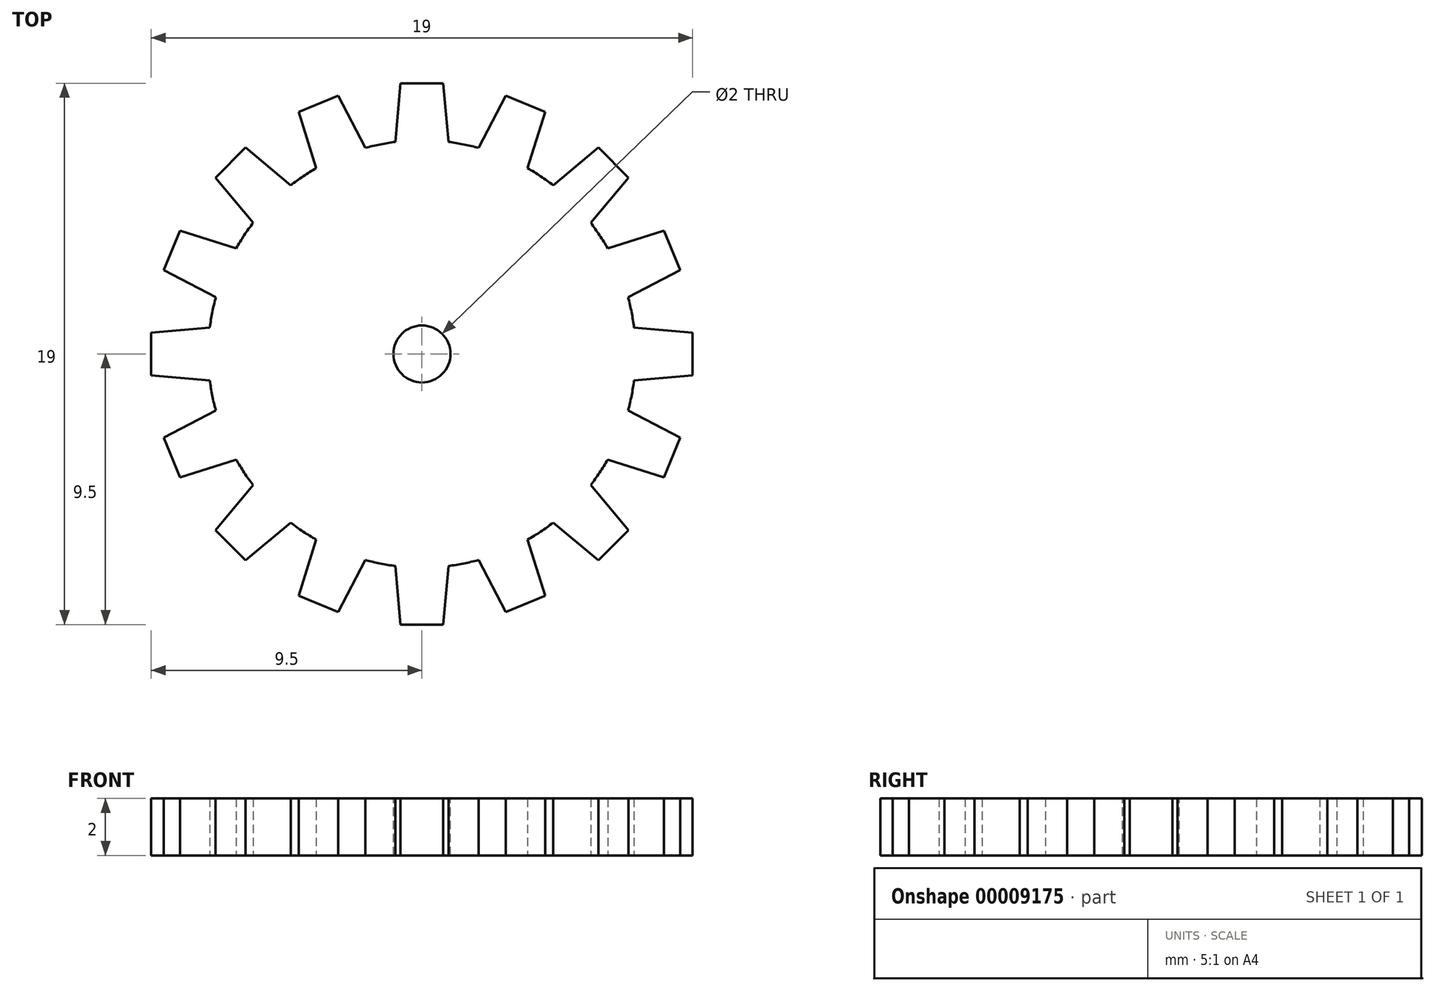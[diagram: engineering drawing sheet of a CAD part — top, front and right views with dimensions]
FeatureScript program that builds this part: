
annotation { "Feature Type Name" : "Feature", "Feature Type Description" : "" }
export const myFeature = defineFeature(function(context is Context, id is Id, definition is map)
    precondition{}
    {
        {
            var Q0;
            Q0=qCreatedBy(makeId("Top.planeOp"),FACE);
            var sketch = newSketch(context, id + "F0", { "sketchPlane" : qUnion([Q0])});
            skCircle(sketch, "E0", {"center": v(0, 0) * mm, "radius": 7.5 * mm});
            skLineSegment(sketch, "E1", {"start": v(0, 0) * mm, "end": v(0, 7.5) * mm, "construction": true});
            skLineSegment(sketch, "E2", {"start": v(-0.93, 7.44) * mm, "end": v(-0.75, 9.5) * mm});
            skLineSegment(sketch, "E3", {"start": v(-0.75, 9.5) * mm, "end": v(0, 9.5) * mm});
            skLineSegment(sketch, "E4.MirrorCS", {"start": v(0.93, 7.44) * mm, "end": v(0.75, 9.5) * mm});
            skLineSegment(sketch, "E5.MirrorCS", {"start": v(0.75, 9.5) * mm, "end": v(0, 9.5) * mm});
            skLineSegment(sketch, "E6.1.0", {"start": v(-3.7, 6.52) * mm, "end": v(-4.33, 8.49) * mm});
            skLineSegment(sketch, "E6.1.1", {"start": v(-4.33, 8.49) * mm, "end": v(-3.64, 8.78) * mm});
            skLineSegment(sketch, "E6.1.2", {"start": v(-2.94, 9.06) * mm, "end": v(-3.64, 8.78) * mm});
            skLineSegment(sketch, "E6.1.3", {"start": v(-1.99, 7.23) * mm, "end": v(-2.94, 9.06) * mm});
            skLineSegment(sketch, "E6.2.0", {"start": v(-5.92, 4.6) * mm, "end": v(-7.25, 6.19) * mm});
            skLineSegment(sketch, "E6.2.1", {"start": v(-7.25, 6.19) * mm, "end": v(-6.72, 6.72) * mm});
            skLineSegment(sketch, "E6.2.2", {"start": v(-6.19, 7.25) * mm, "end": v(-6.72, 6.72) * mm});
            skLineSegment(sketch, "E6.2.3", {"start": v(-4.6, 5.92) * mm, "end": v(-6.19, 7.25) * mm});
            skLineSegment(sketch, "E6.3.0", {"start": v(-7.23, 1.99) * mm, "end": v(-9.06, 2.94) * mm});
            skLineSegment(sketch, "E6.3.1", {"start": v(-9.06, 2.94) * mm, "end": v(-8.78, 3.64) * mm});
            skLineSegment(sketch, "E6.3.2", {"start": v(-8.49, 4.33) * mm, "end": v(-8.78, 3.64) * mm});
            skLineSegment(sketch, "E6.3.3", {"start": v(-6.52, 3.7) * mm, "end": v(-8.49, 4.33) * mm});
            skLineSegment(sketch, "E6.4.0", {"start": v(-7.44, -0.93) * mm, "end": v(-9.5, -0.75) * mm});
            skLineSegment(sketch, "E6.4.1", {"start": v(-9.5, -0.75) * mm, "end": v(-9.5, 0) * mm});
            skLineSegment(sketch, "E6.4.2", {"start": v(-9.5, 0.75) * mm, "end": v(-9.5, 0) * mm});
            skLineSegment(sketch, "E6.4.3", {"start": v(-7.44, 0.93) * mm, "end": v(-9.5, 0.75) * mm});
            skLineSegment(sketch, "E6.5.0", {"start": v(-6.52, -3.7) * mm, "end": v(-8.49, -4.33) * mm});
            skLineSegment(sketch, "E6.5.1", {"start": v(-8.49, -4.33) * mm, "end": v(-8.78, -3.64) * mm});
            skLineSegment(sketch, "E6.5.2", {"start": v(-9.06, -2.94) * mm, "end": v(-8.78, -3.64) * mm});
            skLineSegment(sketch, "E6.5.3", {"start": v(-7.23, -1.99) * mm, "end": v(-9.06, -2.94) * mm});
            skLineSegment(sketch, "E6.6.0", {"start": v(-4.6, -5.92) * mm, "end": v(-6.19, -7.25) * mm});
            skLineSegment(sketch, "E6.6.1", {"start": v(-6.19, -7.25) * mm, "end": v(-6.72, -6.72) * mm});
            skLineSegment(sketch, "E6.6.2", {"start": v(-7.25, -6.19) * mm, "end": v(-6.72, -6.72) * mm});
            skLineSegment(sketch, "E6.6.3", {"start": v(-5.92, -4.6) * mm, "end": v(-7.25, -6.19) * mm});
            skLineSegment(sketch, "E6.7.0", {"start": v(-1.99, -7.23) * mm, "end": v(-2.94, -9.06) * mm});
            skLineSegment(sketch, "E6.7.1", {"start": v(-2.94, -9.06) * mm, "end": v(-3.64, -8.78) * mm});
            skLineSegment(sketch, "E6.7.2", {"start": v(-4.33, -8.49) * mm, "end": v(-3.64, -8.78) * mm});
            skLineSegment(sketch, "E6.7.3", {"start": v(-3.7, -6.52) * mm, "end": v(-4.33, -8.49) * mm});
            skLineSegment(sketch, "E6.8.0", {"start": v(0.93, -7.44) * mm, "end": v(0.75, -9.5) * mm});
            skLineSegment(sketch, "E6.8.1", {"start": v(0.75, -9.5) * mm, "end": v(0, -9.5) * mm});
            skLineSegment(sketch, "E6.8.2", {"start": v(-0.75, -9.5) * mm, "end": v(0, -9.5) * mm});
            skLineSegment(sketch, "E6.8.3", {"start": v(-0.93, -7.44) * mm, "end": v(-0.75, -9.5) * mm});
            skLineSegment(sketch, "E6.9.0", {"start": v(3.7, -6.52) * mm, "end": v(4.33, -8.49) * mm});
            skLineSegment(sketch, "E6.9.1", {"start": v(4.33, -8.49) * mm, "end": v(3.64, -8.78) * mm});
            skLineSegment(sketch, "E6.9.2", {"start": v(2.94, -9.06) * mm, "end": v(3.64, -8.78) * mm});
            skLineSegment(sketch, "E6.9.3", {"start": v(1.99, -7.23) * mm, "end": v(2.94, -9.06) * mm});
            skLineSegment(sketch, "E6.10.0", {"start": v(5.92, -4.6) * mm, "end": v(7.25, -6.19) * mm});
            skLineSegment(sketch, "E6.10.1", {"start": v(7.25, -6.19) * mm, "end": v(6.72, -6.72) * mm});
            skLineSegment(sketch, "E6.10.2", {"start": v(6.19, -7.25) * mm, "end": v(6.72, -6.72) * mm});
            skLineSegment(sketch, "E6.10.3", {"start": v(4.6, -5.92) * mm, "end": v(6.19, -7.25) * mm});
            skLineSegment(sketch, "E6.11.0", {"start": v(7.23, -1.99) * mm, "end": v(9.06, -2.94) * mm});
            skLineSegment(sketch, "E6.11.1", {"start": v(9.06, -2.94) * mm, "end": v(8.78, -3.64) * mm});
            skLineSegment(sketch, "E6.11.2", {"start": v(8.49, -4.33) * mm, "end": v(8.78, -3.64) * mm});
            skLineSegment(sketch, "E6.11.3", {"start": v(6.52, -3.7) * mm, "end": v(8.49, -4.33) * mm});
            skLineSegment(sketch, "E6.12.0", {"start": v(7.44, 0.93) * mm, "end": v(9.5, 0.75) * mm});
            skLineSegment(sketch, "E6.12.1", {"start": v(9.5, 0.75) * mm, "end": v(9.5, 0) * mm});
            skLineSegment(sketch, "E6.12.2", {"start": v(9.5, -0.75) * mm, "end": v(9.5, 0) * mm});
            skLineSegment(sketch, "E6.12.3", {"start": v(7.44, -0.93) * mm, "end": v(9.5, -0.75) * mm});
            skLineSegment(sketch, "E6.13.0", {"start": v(6.52, 3.7) * mm, "end": v(8.49, 4.33) * mm});
            skLineSegment(sketch, "E6.13.1", {"start": v(8.49, 4.33) * mm, "end": v(8.78, 3.64) * mm});
            skLineSegment(sketch, "E6.13.2", {"start": v(9.06, 2.94) * mm, "end": v(8.78, 3.64) * mm});
            skLineSegment(sketch, "E6.13.3", {"start": v(7.23, 1.99) * mm, "end": v(9.06, 2.94) * mm});
            skLineSegment(sketch, "E6.14.0", {"start": v(4.6, 5.92) * mm, "end": v(6.19, 7.25) * mm});
            skLineSegment(sketch, "E6.14.1", {"start": v(6.19, 7.25) * mm, "end": v(6.72, 6.72) * mm});
            skLineSegment(sketch, "E6.14.2", {"start": v(7.25, 6.19) * mm, "end": v(6.72, 6.72) * mm});
            skLineSegment(sketch, "E6.14.3", {"start": v(5.92, 4.6) * mm, "end": v(7.25, 6.19) * mm});
            skLineSegment(sketch, "E6.15.0", {"start": v(1.99, 7.23) * mm, "end": v(2.94, 9.06) * mm});
            skLineSegment(sketch, "E6.15.1", {"start": v(2.94, 9.06) * mm, "end": v(3.64, 8.78) * mm});
            skLineSegment(sketch, "E6.15.2", {"start": v(4.33, 8.49) * mm, "end": v(3.64, 8.78) * mm});
            skLineSegment(sketch, "E6.15.3", {"start": v(3.7, 6.52) * mm, "end": v(4.33, 8.49) * mm});
            skSolve(sketch);
        }
        {
            var Q0;
            Q0 = qSketchRegion(id + "F0", true);
            extrude(context, id + "F1", {"entities" : qUnion([Q0]), "depth" : 2 * mm});
        }
        {
            var Q0;
            Q0=makeQuery(id+"F1.opExtrude","CAP_FACE",FACE,{"disambiguationData":[OSD([sQuery(id+"F0.wireOp",EDGE,"E0"),sQuery(id+"F0.wireOp",EDGE,"E2"),sQuery(id+"F0.wireOp",EDGE,"E3"),sQuery(id+"F0.wireOp",EDGE,"E4.MirrorCS"),sQuery(id+"F0.wireOp",EDGE,"E5.MirrorCS"),sQuery(id+"F0.wireOp",EDGE,"E6.1.0"),sQuery(id+"F0.wireOp",EDGE,"E6.1.1"),sQuery(id+"F0.wireOp",EDGE,"E6.1.2"),sQuery(id+"F0.wireOp",EDGE,"E6.1.3"),sQuery(id+"F0.wireOp",EDGE,"E6.2.0"),sQuery(id+"F0.wireOp",EDGE,"E6.2.1"),sQuery(id+"F0.wireOp",EDGE,"E6.2.2"),sQuery(id+"F0.wireOp",EDGE,"E6.2.3"),sQuery(id+"F0.wireOp",EDGE,"E6.3.0"),sQuery(id+"F0.wireOp",EDGE,"E6.3.1"),sQuery(id+"F0.wireOp",EDGE,"E6.3.2"),sQuery(id+"F0.wireOp",EDGE,"E6.3.3"),sQuery(id+"F0.wireOp",EDGE,"E6.4.0"),sQuery(id+"F0.wireOp",EDGE,"E6.4.1"),sQuery(id+"F0.wireOp",EDGE,"E6.4.2"),sQuery(id+"F0.wireOp",EDGE,"E6.4.3"),sQuery(id+"F0.wireOp",EDGE,"E6.5.0"),sQuery(id+"F0.wireOp",EDGE,"E6.5.1"),sQuery(id+"F0.wireOp",EDGE,"E6.5.2"),sQuery(id+"F0.wireOp",EDGE,"E6.5.3"),sQuery(id+"F0.wireOp",EDGE,"E6.6.0"),sQuery(id+"F0.wireOp",EDGE,"E6.6.1"),sQuery(id+"F0.wireOp",EDGE,"E6.6.2"),sQuery(id+"F0.wireOp",EDGE,"E6.6.3"),sQuery(id+"F0.wireOp",EDGE,"E6.7.0"),sQuery(id+"F0.wireOp",EDGE,"E6.7.1"),sQuery(id+"F0.wireOp",EDGE,"E6.7.2"),sQuery(id+"F0.wireOp",EDGE,"E6.7.3"),sQuery(id+"F0.wireOp",EDGE,"E6.8.0"),sQuery(id+"F0.wireOp",EDGE,"E6.8.1"),sQuery(id+"F0.wireOp",EDGE,"E6.8.2"),sQuery(id+"F0.wireOp",EDGE,"E6.8.3"),sQuery(id+"F0.wireOp",EDGE,"E6.9.0"),sQuery(id+"F0.wireOp",EDGE,"E6.9.1"),sQuery(id+"F0.wireOp",EDGE,"E6.9.2"),sQuery(id+"F0.wireOp",EDGE,"E6.9.3"),sQuery(id+"F0.wireOp",EDGE,"E6.10.0"),sQuery(id+"F0.wireOp",EDGE,"E6.10.1"),sQuery(id+"F0.wireOp",EDGE,"E6.10.2"),sQuery(id+"F0.wireOp",EDGE,"E6.10.3"),sQuery(id+"F0.wireOp",EDGE,"E6.11.0"),sQuery(id+"F0.wireOp",EDGE,"E6.11.1"),sQuery(id+"F0.wireOp",EDGE,"E6.11.2"),sQuery(id+"F0.wireOp",EDGE,"E6.11.3"),sQuery(id+"F0.wireOp",EDGE,"E6.12.0"),sQuery(id+"F0.wireOp",EDGE,"E6.12.1"),sQuery(id+"F0.wireOp",EDGE,"E6.12.2"),sQuery(id+"F0.wireOp",EDGE,"E6.12.3"),sQuery(id+"F0.wireOp",EDGE,"E6.13.0"),sQuery(id+"F0.wireOp",EDGE,"E6.13.1"),sQuery(id+"F0.wireOp",EDGE,"E6.13.2"),sQuery(id+"F0.wireOp",EDGE,"E6.13.3"),sQuery(id+"F0.wireOp",EDGE,"E6.14.0"),sQuery(id+"F0.wireOp",EDGE,"E6.14.1"),sQuery(id+"F0.wireOp",EDGE,"E6.14.2"),sQuery(id+"F0.wireOp",EDGE,"E6.14.3"),sQuery(id+"F0.wireOp",EDGE,"E6.15.0"),sQuery(id+"F0.wireOp",EDGE,"E6.15.1"),sQuery(id+"F0.wireOp",EDGE,"E6.15.2"),sQuery(id+"F0.wireOp",EDGE,"E6.15.3")])],"isStart":false});
            var sketch = newSketch(context, id + "F2", { "sketchPlane" : qUnion([Q0])});
            skCircle(sketch, "E7", {"center": v(0, 0) * mm, "radius": 1 * mm});
            skSolve(sketch);
        }
        {
            var Q0;
            Q0 = qSketchRegion(id + "F2", true);
            extrude(context, id + "F3", {"entities" : qUnion([Q0]), "operationType" : NewBodyOperationType.REMOVE, "endBound" : BoundingType.THROUGH_ALL, "oppositeDirection" : true, "depth" : 25 * mm});
        }
    });
